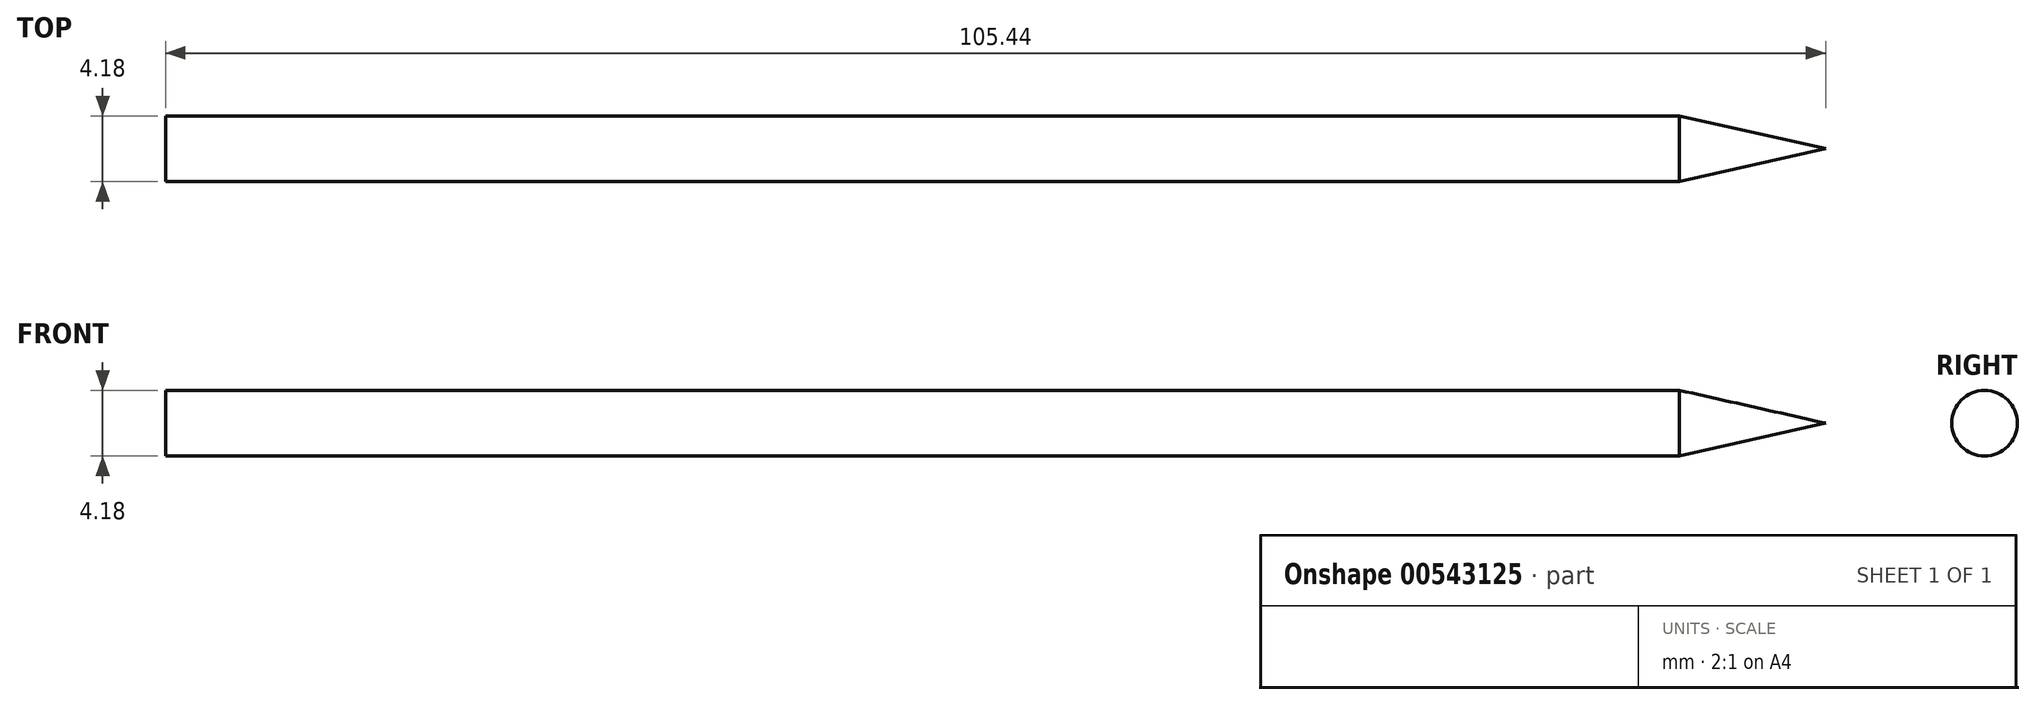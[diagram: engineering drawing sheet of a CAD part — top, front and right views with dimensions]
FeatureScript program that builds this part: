
annotation { "Feature Type Name" : "Feature", "Feature Type Description" : "" }
export const myFeature = defineFeature(function(context is Context, id is Id, definition is map)
    precondition{}
    {
        {
            var Q0;
            Q0=qCreatedBy(makeId("Front.planeOp"),FACE);
            var sketch = newSketch(context, id + "F0", { "sketchPlane" : qUnion([Q0])});
            skLineSegment(sketch, "E0", {"start": v(0, 0) * mm, "end": v(57.37, 0) * mm});
            skLineSegment(sketch, "E1", {"start": v(48.09, 2.09) * mm, "end": v(57.37, 0) * mm});
            skLineSegment(sketch, "E2", {"start": v(57.37, 0) * mm, "end": v(48.09, -2.08) * mm});
            skLineSegment(sketch, "E3", {"start": v(48.09, -2.08) * mm, "end": v(48.09, 2.09) * mm});
            skLineSegment(sketch, "E4", {"start": v(0, 0) * mm, "end": v(-48.07, 0) * mm});
            skLineSegment(sketch, "E5", {"start": v(-48.07, 0) * mm, "end": v(57.37, 0) * mm});
            skLineSegment(sketch, "E6", {"start": v(-48.07, 0) * mm, "end": v(-48.07, 2.08) * mm});
            skLineSegment(sketch, "E7", {"start": v(-48.07, 2.08) * mm, "end": v(48.09, 2.09) * mm});
            skSolve(sketch);
        }
        {
            var Q0;
            {var subQ4=sQuery(id+"F0.wireOp",EDGE,"E6");Q0=makeQuery(id+"F0.imprint","IMPRINT",FACE,{"disambiguationData":[TD([[makeQuery(id+"F0.imprint","IMPRINT",EDGE,{"derivedFrom":subQ4}),-1.0]])]});}
            var Q1;
            Q1=sQuery(id+"F0.wireOp",EDGE,"E5");
            revolve(context, id + "F1", {"entities" : qUnion([Q0]), "axis" : qUnion([Q1]), "revolveType" : RevolveType.SYMMETRIC, "oppositeDirection" : true, "angle" : 360 * degree});
        }
        {
            var Q0;
            {var subQ0=sQuery(id+"F0.wireOp",EDGE,"E1");Q0=makeQuery(id+"F0.imprint","IMPRINT",FACE,{"disambiguationData":[TD([[makeQuery(id+"F0.imprint","IMPRINT",EDGE,{"derivedFrom":subQ0}),-1.0]])]});}
            var Q1;
            Q1=sQuery(id+"F0.wireOp",EDGE,"E5");
            revolve(context, id + "F2", {"operationType" : NewBodyOperationType.ADD, "entities" : qUnion([Q0]), "axis" : qUnion([Q1]), "revolveType" : RevolveType.FULL});
        }
    });
